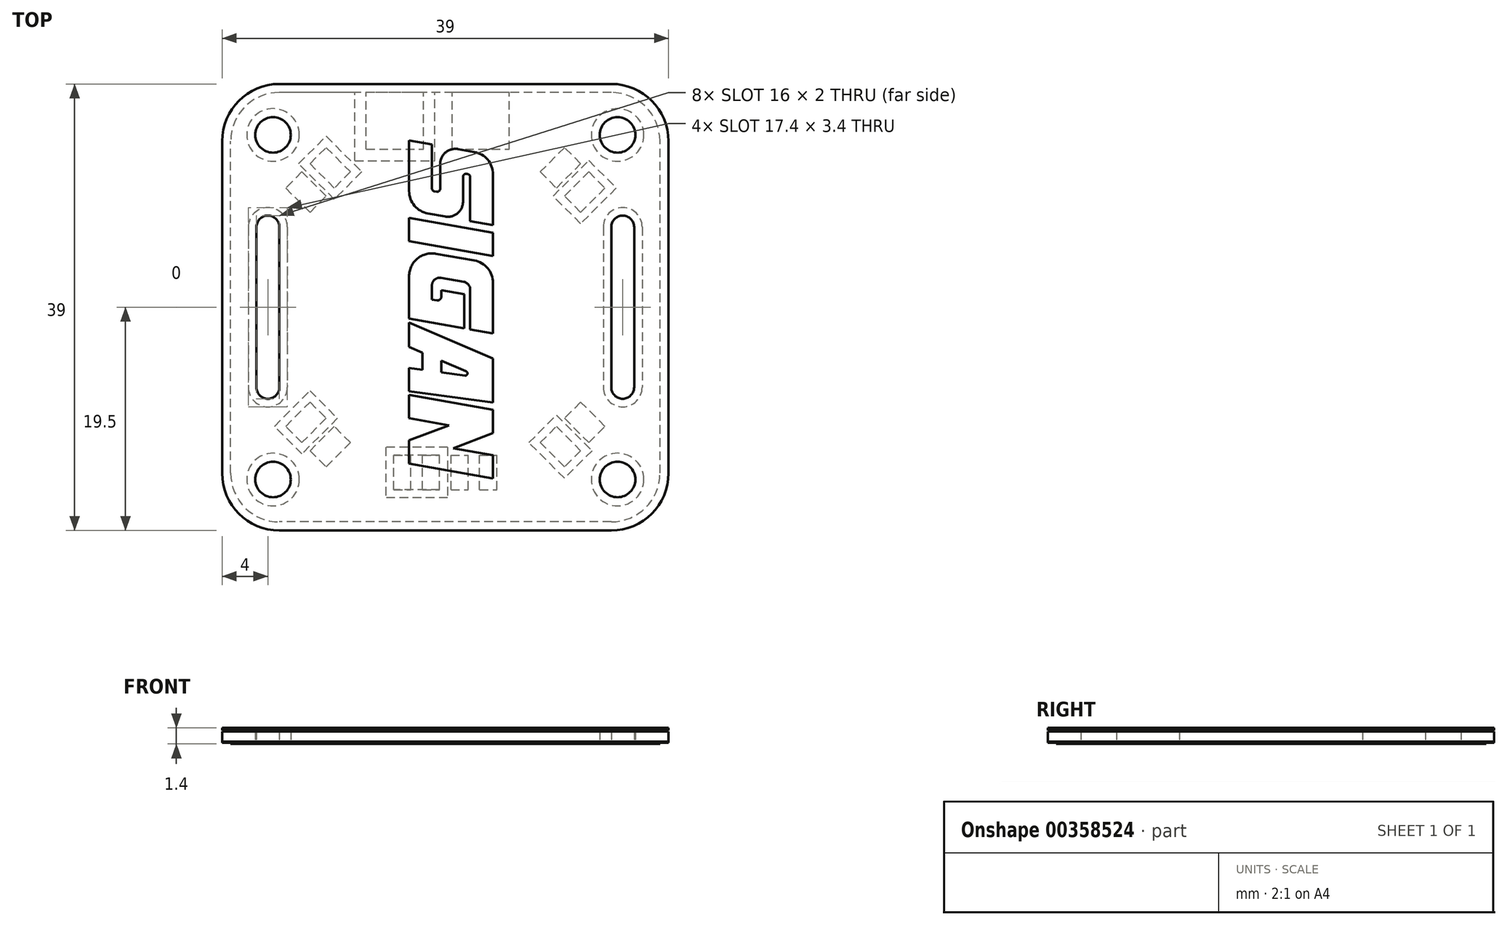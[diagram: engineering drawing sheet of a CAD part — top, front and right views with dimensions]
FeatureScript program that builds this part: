
annotation { "Feature Type Name" : "Feature", "Feature Type Description" : "" }
export const myFeature = defineFeature(function(context is Context, id is Id, definition is map)
    precondition{}
    {
        {
            var Q0;
            Q0=qCreatedBy(makeId("Top.planeOp"),FACE);
            var sketch = newSketch(context, id + "F0", { "sketchPlane" : qUnion([Q0])});
            skLineSegment(sketch, "E0.bottom", {"start": v(14.5, -19.5) * mm, "end": v(-14.5, -19.5) * mm});
            skLineSegment(sketch, "E0.top", {"start": v(14.5, 19.5) * mm, "end": v(7.5, 19.5) * mm});
            skLineSegment(sketch, "E0.left", {"start": v(19.5, -14.5) * mm, "end": v(19.5, 14.5) * mm});
            skLineSegment(sketch, "E0.right", {"start": v(-19.5, -14.5) * mm, "end": v(-19.5, 14.5) * mm});
            skPoint(sketch, "E0.middle", {"position": v(0, 0) * mm});
            skPoint(sketch, "E1.visualSharp", {"position": v(19.5, -19.5) * mm});
            skArc(sketch, "E1.filletArc", {"start": v(14.5, -19.5) * mm, "mid": v(18.04, -18.04) * mm, "end": v(19.5, -14.5) * mm});
            skPoint(sketch, "E2.visualSharp", {"position": v(-19.5, -19.5) * mm});
            skArc(sketch, "E2.filletArc", {"start": v(-19.5, -14.5) * mm, "mid": v(-18.04, -18.04) * mm, "end": v(-14.5, -19.5) * mm});
            skPoint(sketch, "E3.visualSharp", {"position": v(-19.5, 19.5) * mm});
            skArc(sketch, "E3.filletArc", {"start": v(-14.5, 19.5) * mm, "mid": v(-18.04, 18.04) * mm, "end": v(-19.5, 14.5) * mm});
            skPoint(sketch, "E4.visualSharp", {"position": v(19.5, 19.5) * mm});
            skArc(sketch, "E4.filletArc", {"start": v(19.5, 14.5) * mm, "mid": v(18.04, 18.04) * mm, "end": v(14.5, 19.5) * mm});
            skLineSegment(sketch, "E5", {"start": v(-7.5, 19.5) * mm, "end": v(-7.5, 19.5) * mm});
            skLineSegment(sketch, "E6", {"start": v(-7.5, 19.5) * mm, "end": v(7.5, 19.5) * mm});
            skLineSegment(sketch, "E7", {"start": v(7.5, 19.5) * mm, "end": v(7.5, 19.5) * mm});
            skLineSegment(sketch, "E8.trimOffspring", {"start": v(-7.5, 19.5) * mm, "end": v(-14.5, 19.5) * mm});
            skLineSegment(sketch, "E9", {"start": v(0, 19.5) * mm, "end": v(0, 0) * mm, "construction": true});
            skLineSegment(sketch, "E10.left", {"start": v(-16.5, 7) * mm, "end": v(-16.5, -7) * mm});
            skLineSegment(sketch, "E10.right", {"start": v(-14.5, 7) * mm, "end": v(-14.5, -7) * mm});
            skPoint(sketch, "E10.middle", {"position": v(-15.5, 0) * mm});
            skArc(sketch, "E11", {"start": v(-14.5, 7) * mm, "mid": v(-15.5, 8) * mm, "end": v(-16.5, 7) * mm});
            skArc(sketch, "E12", {"start": v(-16.5, -7) * mm, "mid": v(-15.5, -8) * mm, "end": v(-14.5, -7) * mm});
            skArc(sketch, "E13.MirrorCS", {"start": v(16.5, -7) * mm, "mid": v(15.5, -8) * mm, "end": v(14.5, -7) * mm});
            skArc(sketch, "E14.MirrorCS", {"start": v(14.5, 7) * mm, "mid": v(15.5, 8) * mm, "end": v(16.5, 7) * mm});
            skPoint(sketch, "E15.MirrorP", {"position": v(15.5, 0) * mm});
            skLineSegment(sketch, "E16.MirrorCS", {"start": v(16.5, 7) * mm, "end": v(16.5, -7) * mm});
            skLineSegment(sketch, "E17.MirrorCS", {"start": v(14.5, 7) * mm, "end": v(14.5, -7) * mm});
            skCircle(sketch, "E18.0", {"center": v(-15.05, 15.05) * mm, "radius": 1.55 * mm});
            skCircle(sketch, "E18.1", {"center": v(15.05, 15.05) * mm, "radius": 1.55 * mm});
            skCircle(sketch, "E18.2", {"center": v(15.05, -15.05) * mm, "radius": 1.55 * mm});
            skCircle(sketch, "E18.3", {"center": v(-15.05, -15.05) * mm, "radius": 1.55 * mm});
            skSolve(sketch);
        }
        {
            var Q0;
            {var subQ0=makeQuery(id+"FaKBFoj8S7sMaQz_0.opExtrude","CAP_EDGE",EDGE,{"disambiguationData":[OSD([sQuery(id+"FUyg42RqR56omhc_0.wireOp",EDGE,"1f71cb04-1cd7-49c8-8af8-68a2ebdd6a70.filletArc")])],"isStart":true});Q0=makeQuery(id+"F0.imprint","IMPRINT",FACE,{"disambiguationData":[TD([[makeQuery(id+"F0.imprint","IMPRINT",EDGE,{"derivedFrom":subQ0}),-1.0]])]});}
            var Q1;
            Q1=makeQuery(id+"F0.imprint","IMPRINT",FACE,{"disambiguationData":[TD([[makeQuery(id+"F0.imprint","IMPRINT",EDGE,{"derivedFrom":sQuery(id+"F0.wireOp",EDGE,"E0.bottom")}),-1.0]])]});
            var Q2;
            {var subQ0=makeQuery(id+"FaKBFoj8S7sMaQz_0.opExtrude","CAP_EDGE",EDGE,{"disambiguationData":[OSD([sQuery(id+"FUyg42RqR56omhc_0.wireOp",EDGE,"45a09e78-3408-4181-94d1-7675ea45a7b5.0")])],"isStart":true});Q2=makeQuery(id+"F0.imprint","IMPRINT",FACE,{"disambiguationData":[TD([[makeQuery(id+"F0.imprint","IMPRINT",EDGE,{"derivedFrom":subQ0}),1.0]])]});}
            extrude(context, id + "F1", {"entities" : qUnion([Q0, Q1, Q2]), "depth" : 1 * mm});
        }
        {
            var Q0;
            Q0=makeQuery(id+"F1.opExtrude","SWEPT_BODY",BODY,{"disambiguationData":[OSD([sQuery(id+"FUyg42RqR56omhc_0.wireOp",EDGE,"apNCEg5n-BcgS-b9KA-570i-48yKU28l5lF8"),sQuery(id+"F0.wireOp",EDGE,"E0.bottom"),sQuery(id+"F0.wireOp",EDGE,"E0.top"),sQuery(id+"F0.wireOp",EDGE,"E0.left"),sQuery(id+"F0.wireOp",EDGE,"E0.right"),sQuery(id+"F0.wireOp",EDGE,"E1.filletArc"),sQuery(id+"F0.wireOp",EDGE,"E2.filletArc"),sQuery(id+"F0.wireOp",EDGE,"E3.filletArc"),sQuery(id+"F0.wireOp",EDGE,"E4.filletArc")])]});
            var Q1;
            Q1=qCreatedBy(makeId("Top.planeOp"),FACE);
            transform(context, id + "F2", {"entities" : qUnion([Q0]), "transformType" : TransformType.TRANSLATION_DISTANCE, "transformDirection" : qUnion([Q1]), "distance" : 6 * mm, "oppositeDirection" : true, "makeCopy" : false});
        }
        {
            var Q0;
            Q0=makeQuery(id+"F1.opExtrude","CAP_FACE",FACE,{"disambiguationData":[OSD([sQuery(id+"FUyg42RqR56omhc_0.wireOp",EDGE,"apNCEg5n-BcgS-b9KA-570i-48yKU28l5lF8"),sQuery(id+"F0.wireOp",EDGE,"E0.bottom"),sQuery(id+"F0.wireOp",EDGE,"E0.top"),sQuery(id+"F0.wireOp",EDGE,"E0.left"),sQuery(id+"F0.wireOp",EDGE,"E0.right"),sQuery(id+"F0.wireOp",EDGE,"E1.filletArc"),sQuery(id+"F0.wireOp",EDGE,"E2.filletArc"),sQuery(id+"F0.wireOp",EDGE,"E3.filletArc"),sQuery(id+"F0.wireOp",EDGE,"E4.filletArc"),sQuery(id+"F0.wireOp",EDGE,"E5"),sQuery(id+"F0.wireOp",EDGE,"E6"),sQuery(id+"F0.wireOp",EDGE,"E7"),sQuery(id+"F0.wireOp",EDGE,"E8.trimOffspring"),sQuery(id+"F0.wireOp",EDGE,"E10.left"),sQuery(id+"F0.wireOp",EDGE,"E10.right"),sQuery(id+"F0.wireOp",EDGE,"E11"),sQuery(id+"F0.wireOp",EDGE,"E12"),sQuery(id+"F0.wireOp",EDGE,"E13.MirrorCS"),sQuery(id+"F0.wireOp",EDGE,"E14.MirrorCS"),sQuery(id+"F0.wireOp",EDGE,"E16.MirrorCS"),sQuery(id+"F0.wireOp",EDGE,"E17.MirrorCS")])],"isStart":true});
            var sketch = newSketch(context, id + "F3", { "sketchPlane" : qUnion([Q0])});
            skLineSegment(sketch, "E19.bottom", {"start": v(0.6, -13.8) * mm, "end": v(5.6, -13.8) * mm});
            skLineSegment(sketch, "E19.top", {"start": v(0.6, -18.8) * mm, "end": v(5.6, -18.8) * mm});
            skLineSegment(sketch, "E19.left", {"start": v(0.6, -13.8) * mm, "end": v(0.6, -18.8) * mm});
            skLineSegment(sketch, "E19.right", {"start": v(5.6, -13.8) * mm, "end": v(5.6, -18.8) * mm});
            skPoint(sketch, "E19.middle", {"position": v(3.1, -16.3) * mm});
            skLineSegment(sketch, "E20.1.0.0", {"start": v(-1.9, -13.8) * mm, "end": v(-1.9, -18.8) * mm});
            skLineSegment(sketch, "E20.1.0.1", {"start": v(-6.9, -13.8) * mm, "end": v(-1.9, -13.8) * mm});
            skLineSegment(sketch, "E20.1.0.2", {"start": v(-6.9, -18.8) * mm, "end": v(-1.9, -18.8) * mm});
            skLineSegment(sketch, "E20.1.0.3", {"start": v(-6.9, -13.8) * mm, "end": v(-6.9, -18.8) * mm});
            skPoint(sketch, "E20.1.0.4", {"position": v(-4.4, -16.3) * mm});
            skLineSegment(sketch, "E20.direction1", {"start": v(0.6, -18.8) * mm, "end": v(-6.9, -18.8) * mm, "construction": true});
            skLineSegment(sketch, "E21", {"start": v(13.95, -10.41) * mm, "end": v(11.83, -8.29) * mm});
            skLineSegment(sketch, "E22", {"start": v(11.83, -8.29) * mm, "end": v(10.41, -9.7) * mm});
            skLineSegment(sketch, "E23", {"start": v(10.41, -9.7) * mm, "end": v(12.53, -11.83) * mm});
            skLineSegment(sketch, "E24", {"start": v(12.53, -11.83) * mm, "end": v(13.95, -10.41) * mm});
            skPoint(sketch, "E25.center", {"position": v(0, 0) * mm});
            skLineSegment(sketch, "E26", {"start": v(0, 0) * mm, "end": v(0, -24.64) * mm, "construction": true});
            skLineSegment(sketch, "E27", {"start": v(0, 0) * mm, "end": v(21.38, -21.38) * mm, "construction": true});
            skLineSegment(sketch, "E28.MirrorCS", {"start": v(8.29, -11.83) * mm, "end": v(9.7, -10.41) * mm});
            skLineSegment(sketch, "E29.MirrorCS", {"start": v(9.7, -10.41) * mm, "end": v(11.83, -12.53) * mm});
            skLineSegment(sketch, "E30.MirrorCS", {"start": v(10.41, -13.95) * mm, "end": v(8.29, -11.83) * mm});
            skLineSegment(sketch, "E31.MirrorCS", {"start": v(11.83, -12.53) * mm, "end": v(10.41, -13.95) * mm});
            skLineSegment(sketch, "E32.1.0", {"start": v(-8.29, -11.83) * mm, "end": v(-9.7, -10.41) * mm});
            skLineSegment(sketch, "E32.1.1", {"start": v(-11.83, -8.29) * mm, "end": v(-10.41, -9.7) * mm});
            skLineSegment(sketch, "E32.1.2", {"start": v(-10.41, -9.7) * mm, "end": v(-12.53, -11.83) * mm});
            skLineSegment(sketch, "E32.1.3", {"start": v(-9.7, -10.41) * mm, "end": v(-11.83, -12.53) * mm});
            skLineSegment(sketch, "E32.1.4", {"start": v(-11.83, -12.53) * mm, "end": v(-10.41, -13.95) * mm});
            skLineSegment(sketch, "E32.1.5", {"start": v(-12.53, -11.83) * mm, "end": v(-13.95, -10.41) * mm});
            skLineSegment(sketch, "E32.1.6", {"start": v(-10.41, -13.95) * mm, "end": v(-8.29, -11.83) * mm});
            skLineSegment(sketch, "E32.1.7", {"start": v(-13.95, -10.41) * mm, "end": v(-11.83, -8.29) * mm});
            skLineSegment(sketch, "E32.2.0", {"start": v(-11.83, 8.29) * mm, "end": v(-10.41, 9.7) * mm});
            skLineSegment(sketch, "E32.2.1", {"start": v(-8.29, 11.83) * mm, "end": v(-9.7, 10.41) * mm});
            skLineSegment(sketch, "E32.2.2", {"start": v(-9.7, 10.41) * mm, "end": v(-11.83, 12.53) * mm});
            skLineSegment(sketch, "E32.2.3", {"start": v(-10.41, 9.7) * mm, "end": v(-12.53, 11.83) * mm});
            skLineSegment(sketch, "E32.2.4", {"start": v(-12.53, 11.83) * mm, "end": v(-13.95, 10.41) * mm});
            skLineSegment(sketch, "E32.2.5", {"start": v(-11.83, 12.53) * mm, "end": v(-10.41, 13.95) * mm});
            skLineSegment(sketch, "E32.2.6", {"start": v(-13.95, 10.41) * mm, "end": v(-11.83, 8.29) * mm});
            skLineSegment(sketch, "E32.2.7", {"start": v(-10.41, 13.95) * mm, "end": v(-8.29, 11.83) * mm});
            skLineSegment(sketch, "E32.3.0", {"start": v(8.29, 11.83) * mm, "end": v(9.7, 10.41) * mm});
            skLineSegment(sketch, "E32.3.1", {"start": v(11.83, 8.29) * mm, "end": v(10.41, 9.7) * mm});
            skLineSegment(sketch, "E32.3.2", {"start": v(10.41, 9.7) * mm, "end": v(12.53, 11.83) * mm});
            skLineSegment(sketch, "E32.3.3", {"start": v(9.7, 10.41) * mm, "end": v(11.83, 12.53) * mm});
            skLineSegment(sketch, "E32.3.4", {"start": v(11.83, 12.53) * mm, "end": v(10.41, 13.95) * mm});
            skLineSegment(sketch, "E32.3.5", {"start": v(12.53, 11.83) * mm, "end": v(13.95, 10.41) * mm});
            skLineSegment(sketch, "E32.3.6", {"start": v(10.41, 13.95) * mm, "end": v(8.29, 11.83) * mm});
            skLineSegment(sketch, "E32.3.7", {"start": v(13.95, 10.41) * mm, "end": v(11.83, 8.29) * mm});
            skLineSegment(sketch, "E32.anchor1", {"start": v(0, 0) * mm, "end": v(10.41, -13.95) * mm, "construction": true});
            skLineSegment(sketch, "E32.anchor2", {"start": v(0, 0) * mm, "end": v(13.95, 10.41) * mm, "construction": true});
            skLineSegment(sketch, "E33.bottom", {"start": v(3, 15.94) * mm, "end": v(4.5, 15.94) * mm});
            skLineSegment(sketch, "E33.top", {"start": v(3, 12.94) * mm, "end": v(4.5, 12.94) * mm});
            skLineSegment(sketch, "E33.left", {"start": v(3, 15.94) * mm, "end": v(3, 12.94) * mm});
            skLineSegment(sketch, "E33.right", {"start": v(4.5, 15.94) * mm, "end": v(4.5, 12.94) * mm});
            skPoint(sketch, "E33.middle", {"position": v(3.75, 14.44) * mm});
            skPoint(sketch, "E34.1.0.0", {"position": v(1.25, 14.44) * mm});
            skLineSegment(sketch, "E34.1.0.1", {"start": v(0.5, 12.94) * mm, "end": v(2, 12.94) * mm});
            skLineSegment(sketch, "E34.1.0.2", {"start": v(2, 15.94) * mm, "end": v(2, 12.94) * mm});
            skLineSegment(sketch, "E34.1.0.3", {"start": v(0.5, 15.94) * mm, "end": v(0.5, 12.94) * mm});
            skLineSegment(sketch, "E34.1.0.4", {"start": v(0.5, 15.94) * mm, "end": v(2, 15.94) * mm});
            skPoint(sketch, "E34.2.0.0", {"position": v(-1.25, 14.44) * mm});
            skLineSegment(sketch, "E34.2.0.1", {"start": v(-2, 12.94) * mm, "end": v(-0.5, 12.94) * mm});
            skLineSegment(sketch, "E34.2.0.2", {"start": v(-0.5, 15.94) * mm, "end": v(-0.5, 12.94) * mm});
            skLineSegment(sketch, "E34.2.0.3", {"start": v(-2, 15.94) * mm, "end": v(-2, 12.94) * mm});
            skLineSegment(sketch, "E34.2.0.4", {"start": v(-2, 15.94) * mm, "end": v(-0.5, 15.94) * mm});
            skPoint(sketch, "E34.3.0.0", {"position": v(-3.75, 14.44) * mm});
            skLineSegment(sketch, "E34.3.0.1", {"start": v(-4.5, 12.94) * mm, "end": v(-3, 12.94) * mm});
            skLineSegment(sketch, "E34.3.0.2", {"start": v(-3, 15.94) * mm, "end": v(-3, 12.94) * mm});
            skLineSegment(sketch, "E34.3.0.3", {"start": v(-4.5, 15.94) * mm, "end": v(-4.5, 12.94) * mm});
            skLineSegment(sketch, "E34.3.0.4", {"start": v(-4.5, 15.94) * mm, "end": v(-3, 15.94) * mm});
            skLineSegment(sketch, "E34.direction1", {"start": v(3, 12.94) * mm, "end": v(0.5, 12.94) * mm, "construction": true});
            skSolve(sketch);
        }
        {
            var Q0;
            Q0=makeQuery(id+"F3.imprint","IMPRINT",FACE,{"disambiguationData":[TD([[makeQuery(id+"F3.imprint","IMPRINT",EDGE,{"derivedFrom":sQuery(id+"F3.wireOp",EDGE,"E19.bottom")}),1.0]])]});
            extrude(context, id + "F4", {"entities" : qUnion([Q0]), "depth" : .1 * mm});
        }
        {
            var Q0;
            Q0=makeQuery(id+"F1.opExtrude","CAP_FACE",FACE,{"disambiguationData":[OSD([sQuery(id+"FUyg42RqR56omhc_0.wireOp",EDGE,"apNCEg5n-BcgS-b9KA-570i-48yKU28l5lF8"),sQuery(id+"F0.wireOp",EDGE,"E0.bottom"),sQuery(id+"F0.wireOp",EDGE,"E0.top"),sQuery(id+"F0.wireOp",EDGE,"E0.left"),sQuery(id+"F0.wireOp",EDGE,"E0.right"),sQuery(id+"F0.wireOp",EDGE,"E1.filletArc"),sQuery(id+"F0.wireOp",EDGE,"E2.filletArc"),sQuery(id+"F0.wireOp",EDGE,"E3.filletArc"),sQuery(id+"F0.wireOp",EDGE,"E4.filletArc"),sQuery(id+"F0.wireOp",EDGE,"E5"),sQuery(id+"F0.wireOp",EDGE,"E6"),sQuery(id+"F0.wireOp",EDGE,"E7"),sQuery(id+"F0.wireOp",EDGE,"E8.trimOffspring"),sQuery(id+"F0.wireOp",EDGE,"E10.left"),sQuery(id+"F0.wireOp",EDGE,"E10.right"),sQuery(id+"F0.wireOp",EDGE,"E11"),sQuery(id+"F0.wireOp",EDGE,"E12"),sQuery(id+"F0.wireOp",EDGE,"E13.MirrorCS"),sQuery(id+"F0.wireOp",EDGE,"E14.MirrorCS"),sQuery(id+"F0.wireOp",EDGE,"E16.MirrorCS"),sQuery(id+"F0.wireOp",EDGE,"E17.MirrorCS")])],"isStart":true});
            var sketch = newSketch(context, id + "F5", { "sketchPlane" : qUnion([Q0])});
            skLineSegment(sketch, "E35.0", {"start": v(9.42, -9.7) * mm, "end": v(12.53, -12.82) * mm});
            skLineSegment(sketch, "E35.1", {"start": v(11.83, -7.3) * mm, "end": v(9.42, -9.7) * mm});
            skLineSegment(sketch, "E35.2", {"start": v(14.94, -10.41) * mm, "end": v(11.83, -7.3) * mm});
            skLineSegment(sketch, "E35.3", {"start": v(12.53, -12.82) * mm, "end": v(14.94, -10.41) * mm});
            skLineSegment(sketch, "E36.1.0", {"start": v(7.3, 11.83) * mm, "end": v(9.7, 9.42) * mm});
            skLineSegment(sketch, "E36.1.1", {"start": v(9.7, 9.42) * mm, "end": v(12.82, 12.53) * mm});
            skLineSegment(sketch, "E36.1.2", {"start": v(10.41, 14.94) * mm, "end": v(7.3, 11.83) * mm});
            skLineSegment(sketch, "E36.1.3", {"start": v(12.82, 12.53) * mm, "end": v(10.41, 14.94) * mm});
            skLineSegment(sketch, "E36.2.0", {"start": v(-11.83, 7.3) * mm, "end": v(-9.42, 9.7) * mm});
            skLineSegment(sketch, "E36.2.1", {"start": v(-9.42, 9.7) * mm, "end": v(-12.53, 12.82) * mm});
            skLineSegment(sketch, "E36.2.2", {"start": v(-14.94, 10.41) * mm, "end": v(-11.83, 7.3) * mm});
            skLineSegment(sketch, "E36.2.3", {"start": v(-12.53, 12.82) * mm, "end": v(-14.94, 10.41) * mm});
            skLineSegment(sketch, "E36.3.0", {"start": v(-7.3, -11.83) * mm, "end": v(-9.7, -9.42) * mm});
            skLineSegment(sketch, "E36.3.1", {"start": v(-9.7, -9.42) * mm, "end": v(-12.82, -12.53) * mm});
            skLineSegment(sketch, "E36.3.2", {"start": v(-10.41, -14.94) * mm, "end": v(-7.9, -12.43) * mm});
            skLineSegment(sketch, "E36.3.3", {"start": v(-12.82, -12.53) * mm, "end": v(-10.41, -14.94) * mm});
            skPoint(sketch, "E36.center", {"position": v(0, 0) * mm});
            skLineSegment(sketch, "E37.0", {"start": v(-0.9, -12.8) * mm, "end": v(-0.9, -19.5) * mm});
            skLineSegment(sketch, "E37.1", {"start": v(-7.9, -12.8) * mm, "end": v(-0.9, -12.8) * mm});
            skLineSegment(sketch, "E37.2", {"start": v(-7.9, -12.8) * mm, "end": v(-7.9, -19.5) * mm});
            skLineSegment(sketch, "E38.0", {"start": v(14.5, -19.5) * mm, "end": v(-14.5, -19.5) * mm});
            skLineSegment(sketch, "E39.trimOffspring", {"start": v(-7.9, -12.43) * mm, "end": v(-7.3, -11.83) * mm});
            skArc(sketch, "E40.0", {"start": v(18.75, -14.5) * mm, "mid": v(17.5, -17.5) * mm, "end": v(14.5, -18.75) * mm});
            skLineSegment(sketch, "E40.1", {"start": v(18.75, 14.5) * mm, "end": v(18.75, -14.5) * mm});
            skLineSegment(sketch, "E40.2", {"start": v(14.5, -18.75) * mm, "end": v(-14.5, -18.75) * mm});
            skArc(sketch, "E40.3", {"start": v(14.5, 18.75) * mm, "mid": v(17.5, 17.5) * mm, "end": v(18.75, 14.5) * mm});
            skArc(sketch, "E40.4", {"start": v(-14.5, -18.75) * mm, "mid": v(-17.5, -17.5) * mm, "end": v(-18.75, -14.5) * mm});
            skLineSegment(sketch, "E40.5", {"start": v(-18.75, 14.5) * mm, "end": v(-18.75, -14.5) * mm});
            skArc(sketch, "E40.6", {"start": v(-18.75, 14.5) * mm, "mid": v(-17.5, 17.5) * mm, "end": v(-14.5, 18.75) * mm});
            skLineSegment(sketch, "E40.7", {"start": v(14.5, 18.75) * mm, "end": v(-14.5, 18.75) * mm});
            skCircle(sketch, "E41.0", {"center": v(15.05, -15.05) * mm, "radius": 2.3 * mm});
            skCircle(sketch, "E42.0", {"center": v(-15.05, -15.05) * mm, "radius": 2.3 * mm});
            skCircle(sketch, "E43.0", {"center": v(-15.05, 15.05) * mm, "radius": 2.3 * mm});
            skCircle(sketch, "E44.0", {"center": v(15.05, 15.05) * mm, "radius": 2.3 * mm});
            skArc(sketch, "E45.0", {"start": v(13.8, -7) * mm, "mid": v(15.5, -8.7) * mm, "end": v(17.2, -7) * mm});
            skLineSegment(sketch, "E45.1", {"start": v(13.8, -7) * mm, "end": v(13.8, 7) * mm});
            skArc(sketch, "E45.2", {"start": v(17.2, 7) * mm, "mid": v(15.5, 8.7) * mm, "end": v(13.8, 7) * mm});
            skLineSegment(sketch, "E45.3", {"start": v(17.2, -7) * mm, "end": v(17.2, 7) * mm});
            skLineSegment(sketch, "E46.0", {"start": v(-13.8, -7) * mm, "end": v(-13.8, 7) * mm});
            skArc(sketch, "E46.1", {"start": v(-13.8, -7) * mm, "mid": v(-15.5, -8.7) * mm, "end": v(-17.2, -7) * mm});
            skLineSegment(sketch, "E46.2", {"start": v(-17.2, -7) * mm, "end": v(-17.2, 7) * mm});
            skArc(sketch, "E46.3", {"start": v(-17.2, 7) * mm, "mid": v(-15.5, 8.7) * mm, "end": v(-13.8, 7) * mm});
            skLineSegment(sketch, "E47.0", {"start": v(10.41, -9.7) * mm, "end": v(12.53, -11.83) * mm});
            skLineSegment(sketch, "E47.1", {"start": v(12.53, -11.83) * mm, "end": v(13.95, -10.41) * mm});
            skLineSegment(sketch, "E47.2", {"start": v(13.95, -10.41) * mm, "end": v(11.83, -8.29) * mm});
            skLineSegment(sketch, "E47.3", {"start": v(11.83, -8.29) * mm, "end": v(10.41, -9.7) * mm});
            skLineSegment(sketch, "E47.4", {"start": v(-10.41, -13.95) * mm, "end": v(-8.29, -11.83) * mm});
            skLineSegment(sketch, "E47.5", {"start": v(-11.83, -12.53) * mm, "end": v(-10.41, -13.95) * mm});
            skLineSegment(sketch, "E47.6", {"start": v(-9.7, -10.41) * mm, "end": v(-11.83, -12.53) * mm});
            skLineSegment(sketch, "E47.7", {"start": v(-8.29, -11.83) * mm, "end": v(-9.7, -10.41) * mm});
            skLineSegment(sketch, "E47.8", {"start": v(-13.95, 10.41) * mm, "end": v(-11.83, 8.29) * mm});
            skLineSegment(sketch, "E47.9", {"start": v(-11.83, 8.29) * mm, "end": v(-10.41, 9.7) * mm});
            skLineSegment(sketch, "E47.10", {"start": v(-12.53, 11.83) * mm, "end": v(-13.95, 10.41) * mm});
            skLineSegment(sketch, "E47.11", {"start": v(-10.41, 9.7) * mm, "end": v(-12.53, 11.83) * mm});
            skLineSegment(sketch, "E47.12", {"start": v(9.7, 10.41) * mm, "end": v(11.83, 12.53) * mm});
            skLineSegment(sketch, "E47.13", {"start": v(8.29, 11.83) * mm, "end": v(9.7, 10.41) * mm});
            skLineSegment(sketch, "E47.14", {"start": v(10.41, 13.95) * mm, "end": v(8.29, 11.83) * mm});
            skLineSegment(sketch, "E47.15", {"start": v(11.83, 12.53) * mm, "end": v(10.41, 13.95) * mm});
            skLineSegment(sketch, "E48.0", {"start": v(-1.9, -13.8) * mm, "end": v(-1.9, -18.8) * mm});
            skLineSegment(sketch, "E48.1", {"start": v(-6.9, -13.8) * mm, "end": v(-1.9, -13.8) * mm});
            skLineSegment(sketch, "E48.2", {"start": v(-6.9, -13.8) * mm, "end": v(-6.9, -18.8) * mm});
            skLineSegment(sketch, "E48.3", {"start": v(-6.9, -18.8) * mm, "end": v(-1.9, -18.8) * mm});
            skLineSegment(sketch, "E49.bottom", {"start": v(0.2, 12.24) * mm, "end": v(-5.2, 12.24) * mm});
            skLineSegment(sketch, "E49.top", {"start": v(0.2, 16.64) * mm, "end": v(-5.2, 16.64) * mm});
            skLineSegment(sketch, "E49.left", {"start": v(0.2, 12.24) * mm, "end": v(0.2, 16.64) * mm});
            skLineSegment(sketch, "E49.right", {"start": v(-5.2, 12.24) * mm, "end": v(-5.2, 16.64) * mm});
            skLineSegment(sketch, "E50.bottom", {"start": v(-0.5, 12.94) * mm, "end": v(-4.5, 12.94) * mm});
            skLineSegment(sketch, "E50.top", {"start": v(-0.5, 15.94) * mm, "end": v(-4.5, 15.94) * mm});
            skLineSegment(sketch, "E50.left", {"start": v(-0.5, 12.94) * mm, "end": v(-0.5, 15.94) * mm});
            skLineSegment(sketch, "E50.right", {"start": v(-4.5, 12.94) * mm, "end": v(-4.5, 15.94) * mm});
            skSolve(sketch);
        }
        {
            var Q0;
            Q0=makeQuery(id+"F5.imprint","IMPRINT",FACE,{"disambiguationData":[TD([[makeQuery(id+"F5.imprint","IMPRINT",EDGE,{"derivedFrom":sQuery(id+"F5.wireOp",EDGE,"E35.0")}),-1.0]])]});
            var Q1;
            Q1=makeQuery(id+"F5.imprint","IMPRINT",FACE,{"disambiguationData":[TD([[makeQuery(id+"F5.imprint","IMPRINT",EDGE,{"derivedFrom":sQuery(id+"F5.wireOp",EDGE,"E47.0")}),1.0]])]});
            var Q2;
            Q2=makeQuery(id+"F5.imprint","IMPRINT",FACE,{"disambiguationData":[TD([[makeQuery(id+"F5.imprint","IMPRINT",EDGE,{"derivedFrom":sQuery(id+"F5.wireOp",EDGE,"E47.4")}),1.0]])]});
            var Q3;
            Q3=makeQuery(id+"F5.imprint","IMPRINT",FACE,{"disambiguationData":[TD([[makeQuery(id+"F5.imprint","IMPRINT",EDGE,{"derivedFrom":sQuery(id+"F5.wireOp",EDGE,"E47.8")}),1.0]])]});
            var Q4;
            Q4=makeQuery(id+"F5.imprint","IMPRINT",FACE,{"disambiguationData":[TD([[makeQuery(id+"F5.imprint","IMPRINT",EDGE,{"derivedFrom":sQuery(id+"F5.wireOp",EDGE,"E47.12")}),1.0]])]});
            var Q5;
            {var subQ5=sQuery(id+"F5.wireOp",EDGE,"E48.1");Q5=makeQuery(id+"F5.imprint","IMPRINT",FACE,{"disambiguationData":[TD([[makeQuery(id+"F5.imprint","IMPRINT",EDGE,{"derivedFrom":subQ5}),-1.0]])]});}
            var Q6;
            Q6=makeQuery(id+"F5.imprint","IMPRINT",FACE,{"disambiguationData":[TD([[makeQuery(id+"F5.imprint","IMPRINT",EDGE,{"derivedFrom":sQuery(id+"F5.wireOp",EDGE,"E50.bottom")}),-1.0]])]});
            extrude(context, id + "F6", {"entities" : qUnion([Q0, Q1, Q2, Q3, Q4, Q5, Q6]), "depth" : .1 * mm});
        }
        {
            var Q0;
            Q0=makeQuery(id+"F4.opExtrude","SWEPT_BODY",BODY,{"disambiguationData":[OSD([sQuery(id+"FUyg42RqR56omhc_0.wireOp",EDGE,"apNCEg5n-BcgS-b9KA-570i-48yKU28l5lF8"),sQuery(id+"F0.wireOp",EDGE,"E0.bottom"),sQuery(id+"F0.wireOp",EDGE,"E0.top"),sQuery(id+"F0.wireOp",EDGE,"E0.left"),sQuery(id+"F0.wireOp",EDGE,"E0.right"),sQuery(id+"F0.wireOp",EDGE,"E1.filletArc"),sQuery(id+"F0.wireOp",EDGE,"E2.filletArc"),sQuery(id+"F0.wireOp",EDGE,"E3.filletArc"),sQuery(id+"F0.wireOp",EDGE,"E4.filletArc"),sQuery(id+"F0.wireOp",EDGE,"E5"),sQuery(id+"F0.wireOp",EDGE,"E6"),sQuery(id+"F0.wireOp",EDGE,"E7"),sQuery(id+"F0.wireOp",EDGE,"E8.trimOffspring"),sQuery(id+"F0.wireOp",EDGE,"E10.left"),sQuery(id+"F0.wireOp",EDGE,"E10.right"),sQuery(id+"F0.wireOp",EDGE,"E11"),sQuery(id+"F0.wireOp",EDGE,"E12"),sQuery(id+"F0.wireOp",EDGE,"E13.MirrorCS"),sQuery(id+"F0.wireOp",EDGE,"E14.MirrorCS"),sQuery(id+"F0.wireOp",EDGE,"E16.MirrorCS"),sQuery(id+"F0.wireOp",EDGE,"E17.MirrorCS"),sQuery(id+"F3.wireOp",EDGE,"E19.bottom"),sQuery(id+"F3.wireOp",EDGE,"E19.top"),sQuery(id+"F3.wireOp",EDGE,"E19.left"),sQuery(id+"F3.wireOp",EDGE,"E19.right"),sQuery(id+"F3.wireOp",EDGE,"E20.1.0.0"),sQuery(id+"F3.wireOp",EDGE,"E20.1.0.1"),sQuery(id+"F3.wireOp",EDGE,"E20.1.0.2"),sQuery(id+"F3.wireOp",EDGE,"E20.1.0.3"),sQuery(id+"F3.wireOp",EDGE,"E21"),sQuery(id+"F3.wireOp",EDGE,"E22"),sQuery(id+"F3.wireOp",EDGE,"E23"),sQuery(id+"F3.wireOp",EDGE,"E24"),sQuery(id+"F3.wireOp",EDGE,"E28.MirrorCS"),sQuery(id+"F3.wireOp",EDGE,"E29.MirrorCS"),sQuery(id+"F3.wireOp",EDGE,"E30.MirrorCS"),sQuery(id+"F3.wireOp",EDGE,"E31.MirrorCS"),sQuery(id+"F3.wireOp",EDGE,"E32.1.0"),sQuery(id+"F3.wireOp",EDGE,"E32.1.1"),sQuery(id+"F3.wireOp",EDGE,"E32.1.2"),sQuery(id+"F3.wireOp",EDGE,"E32.1.3"),sQuery(id+"F3.wireOp",EDGE,"E32.1.4"),sQuery(id+"F3.wireOp",EDGE,"E32.1.5"),sQuery(id+"F3.wireOp",EDGE,"E32.1.6"),sQuery(id+"F3.wireOp",EDGE,"E32.1.7"),sQuery(id+"F3.wireOp",EDGE,"E32.2.0"),sQuery(id+"F3.wireOp",EDGE,"E32.2.1"),sQuery(id+"F3.wireOp",EDGE,"E32.2.2"),sQuery(id+"F3.wireOp",EDGE,"E32.2.3"),sQuery(id+"F3.wireOp",EDGE,"E32.2.4"),sQuery(id+"F3.wireOp",EDGE,"E32.2.5"),sQuery(id+"F3.wireOp",EDGE,"E32.2.6"),sQuery(id+"F3.wireOp",EDGE,"E32.2.7"),sQuery(id+"F3.wireOp",EDGE,"E32.3.0"),sQuery(id+"F3.wireOp",EDGE,"E32.3.1"),sQuery(id+"F3.wireOp",EDGE,"E32.3.2"),sQuery(id+"F3.wireOp",EDGE,"E32.3.3"),sQuery(id+"F3.wireOp",EDGE,"E32.3.4"),sQuery(id+"F3.wireOp",EDGE,"E32.3.5"),sQuery(id+"F3.wireOp",EDGE,"E32.3.6"),sQuery(id+"F3.wireOp",EDGE,"E32.3.7"),sQuery(id+"F3.wireOp",EDGE,"E33.bottom"),sQuery(id+"F3.wireOp",EDGE,"E33.top"),sQuery(id+"F3.wireOp",EDGE,"E33.left"),sQuery(id+"F3.wireOp",EDGE,"E33.right"),sQuery(id+"F3.wireOp",EDGE,"E34.1.0.1"),sQuery(id+"F3.wireOp",EDGE,"E34.1.0.2"),sQuery(id+"F3.wireOp",EDGE,"E34.1.0.3"),sQuery(id+"F3.wireOp",EDGE,"E34.1.0.4"),sQuery(id+"F3.wireOp",EDGE,"E34.2.0.1"),sQuery(id+"F3.wireOp",EDGE,"E34.2.0.2"),sQuery(id+"F3.wireOp",EDGE,"E34.2.0.3"),sQuery(id+"F3.wireOp",EDGE,"E34.2.0.4"),sQuery(id+"F3.wireOp",EDGE,"E34.3.0.1"),sQuery(id+"F3.wireOp",EDGE,"E34.3.0.2"),sQuery(id+"F3.wireOp",EDGE,"E34.3.0.3"),sQuery(id+"F3.wireOp",EDGE,"E34.3.0.4")])]});
            var Q1;
            Q1=qCreatedBy(makeId("Top.planeOp"),FACE);
            transform(context, id + "F7", {"entities" : qUnion([Q0]), "transformType" : TransformType.TRANSLATION_DISTANCE, "transformDirection" : qUnion([Q1]), "distance" : .1 * mm, "makeCopy" : false});
        }
        {
            var Q0;
            Q0=makeQuery(id+"F1.opExtrude","CAP_FACE",FACE,{"disambiguationData":[OSD([sQuery(id+"FUyg42RqR56omhc_0.wireOp",EDGE,"apNCEg5n-BcgS-b9KA-570i-48yKU28l5lF8"),sQuery(id+"F0.wireOp",EDGE,"E0.bottom"),sQuery(id+"F0.wireOp",EDGE,"E0.top"),sQuery(id+"F0.wireOp",EDGE,"E0.left"),sQuery(id+"F0.wireOp",EDGE,"E0.right"),sQuery(id+"F0.wireOp",EDGE,"E1.filletArc"),sQuery(id+"F0.wireOp",EDGE,"E2.filletArc"),sQuery(id+"F0.wireOp",EDGE,"E3.filletArc"),sQuery(id+"F0.wireOp",EDGE,"E4.filletArc"),sQuery(id+"F0.wireOp",EDGE,"E6"),sQuery(id+"F0.wireOp",EDGE,"E8.trimOffspring"),sQuery(id+"F0.wireOp",EDGE,"E10.left"),sQuery(id+"F0.wireOp",EDGE,"E10.right"),sQuery(id+"F0.wireOp",EDGE,"E11"),sQuery(id+"F0.wireOp",EDGE,"E12"),sQuery(id+"F0.wireOp",EDGE,"E13.MirrorCS"),sQuery(id+"F0.wireOp",EDGE,"E14.MirrorCS"),sQuery(id+"F0.wireOp",EDGE,"E16.MirrorCS"),sQuery(id+"F0.wireOp",EDGE,"E17.MirrorCS")])],"isStart":false});
            var sketch = newSketch(context, id + "F8", { "sketchPlane" : qUnion([Q0])});
            skArc(sketch, "E51.0", {"start": v(-14.5, 18.75) * mm, "mid": v(-17.5, 17.5) * mm, "end": v(-18.75, 14.5) * mm});
            skLineSegment(sketch, "E51.1", {"start": v(14.5, 18.75) * mm, "end": v(-14.5, 18.75) * mm});
            skArc(sketch, "E51.2", {"start": v(18.75, 14.5) * mm, "mid": v(17.5, 17.5) * mm, "end": v(14.5, 18.75) * mm});
            skLineSegment(sketch, "E51.3", {"start": v(18.75, -14.5) * mm, "end": v(18.75, 14.5) * mm});
            skArc(sketch, "E51.4", {"start": v(14.5, -18.75) * mm, "mid": v(17.5, -17.5) * mm, "end": v(18.75, -14.5) * mm});
            skLineSegment(sketch, "E51.5", {"start": v(14.5, -18.75) * mm, "end": v(-14.5, -18.75) * mm});
            skArc(sketch, "E51.6", {"start": v(-18.75, -14.5) * mm, "mid": v(-17.5, -17.5) * mm, "end": v(-14.5, -18.75) * mm});
            skLineSegment(sketch, "E51.7", {"start": v(-18.75, -14.5) * mm, "end": v(-18.75, 14.5) * mm});
            skCircle(sketch, "E51.8", {"center": v(-15.05, -15.05) * mm, "radius": 2.3 * mm});
            skCircle(sketch, "E51.9", {"center": v(-15.05, 15.05) * mm, "radius": 2.3 * mm});
            skCircle(sketch, "E51.10", {"center": v(15.05, 15.05) * mm, "radius": 2.3 * mm});
            skCircle(sketch, "E51.11", {"center": v(15.05, -15.05) * mm, "radius": 2.3 * mm});
            skArc(sketch, "E51.12", {"start": v(17.2, -7) * mm, "mid": v(15.5, -8.7) * mm, "end": v(13.8, -7) * mm});
            skLineSegment(sketch, "E51.13", {"start": v(13.8, 7) * mm, "end": v(13.8, -7) * mm});
            skLineSegment(sketch, "E51.14", {"start": v(17.2, 7) * mm, "end": v(17.2, -7) * mm});
            skArc(sketch, "E51.15", {"start": v(13.8, 7) * mm, "mid": v(15.5, 8.7) * mm, "end": v(17.2, 7) * mm});
            skArc(sketch, "E51.16", {"start": v(-13.8, 7) * mm, "mid": v(-15.5, 8.7) * mm, "end": v(-17.2, 7) * mm});
            skLineSegment(sketch, "E51.17", {"start": v(-13.8, 7) * mm, "end": v(-13.8, -7) * mm});
            skLineSegment(sketch, "E51.18", {"start": v(-17.2, 7) * mm, "end": v(-17.2, -7) * mm});
            skArc(sketch, "E51.19", {"start": v(-17.2, -7) * mm, "mid": v(-15.5, -8.7) * mm, "end": v(-13.8, -7) * mm});
            skSolve(sketch);
        }
        {
            var Q0;
            Q0=qSketchRegion(id+"F8",true);
            extrude(context, id + "F9", {"entities" : qUnion([Q0]), "depth" : .1 * mm});
        }
        {
            var Q0;
            Q0=makeQuery(id+"F9.opExtrude","CAP_FACE",FACE,{"disambiguationData":[OSD([sQuery(id+"F8.wireOp",EDGE,"E51.0"),sQuery(id+"F8.wireOp",EDGE,"E51.1"),sQuery(id+"F8.wireOp",EDGE,"E51.2"),sQuery(id+"F8.wireOp",EDGE,"E51.3"),sQuery(id+"F8.wireOp",EDGE,"E51.4"),sQuery(id+"F8.wireOp",EDGE,"E51.5"),sQuery(id+"F8.wireOp",EDGE,"E51.6"),sQuery(id+"F8.wireOp",EDGE,"E51.7"),sQuery(id+"F8.wireOp",EDGE,"E51.8"),sQuery(id+"F8.wireOp",EDGE,"E51.9"),sQuery(id+"F8.wireOp",EDGE,"E51.10"),sQuery(id+"F8.wireOp",EDGE,"E51.11"),sQuery(id+"F8.wireOp",EDGE,"E51.12"),sQuery(id+"F8.wireOp",EDGE,"E51.13"),sQuery(id+"F8.wireOp",EDGE,"E51.14"),sQuery(id+"F8.wireOp",EDGE,"E51.15"),sQuery(id+"F8.wireOp",EDGE,"E51.16"),sQuery(id+"F8.wireOp",EDGE,"E51.17"),sQuery(id+"F8.wireOp",EDGE,"E51.18"),sQuery(id+"F8.wireOp",EDGE,"E51.19")])],"isStart":false});
            var sketch = newSketch(context, id + "F10", { "sketchPlane" : qUnion([Q0])});
            skLineSegment(sketch, "E52.0", {"start": v(14.5, 19.5) * mm, "end": v(-14.5, 19.5) * mm});
            skArc(sketch, "E52.1", {"start": v(-14.5, 19.5) * mm, "mid": v(-18.04, 18.04) * mm, "end": v(-19.5, 14.5) * mm});
            skLineSegment(sketch, "E52.2", {"start": v(-19.5, -14.5) * mm, "end": v(-19.5, 14.5) * mm});
            skArc(sketch, "E52.3", {"start": v(-19.5, -14.5) * mm, "mid": v(-18.04, -18.04) * mm, "end": v(-14.5, -19.5) * mm});
            skLineSegment(sketch, "E52.4", {"start": v(14.5, -19.5) * mm, "end": v(-14.5, -19.5) * mm});
            skArc(sketch, "E52.5", {"start": v(14.5, -19.5) * mm, "mid": v(18.04, -18.04) * mm, "end": v(19.5, -14.5) * mm});
            skLineSegment(sketch, "E52.6", {"start": v(19.5, -14.5) * mm, "end": v(19.5, 14.5) * mm});
            skArc(sketch, "E52.7", {"start": v(19.5, 14.5) * mm, "mid": v(18.04, 18.04) * mm, "end": v(14.5, 19.5) * mm});
            skCircle(sketch, "E53.0", {"center": v(-15.05, 15.05) * mm, "radius": 1.55 * mm});
            skCircle(sketch, "E53.1", {"center": v(15.05, 15.05) * mm, "radius": 1.55 * mm});
            skCircle(sketch, "E53.2", {"center": v(-15.05, -15.05) * mm, "radius": 1.55 * mm});
            skLineSegment(sketch, "E54.0", {"start": v(-14.5, 7) * mm, "end": v(-14.5, -7) * mm});
            skArc(sketch, "E54.1", {"start": v(-14.5, 7) * mm, "mid": v(-15.5, 8) * mm, "end": v(-16.5, 7) * mm});
            skLineSegment(sketch, "E54.2", {"start": v(-16.5, 7) * mm, "end": v(-16.5, -7) * mm});
            skArc(sketch, "E54.3", {"start": v(-16.5, -7) * mm, "mid": v(-15.5, -8) * mm, "end": v(-14.5, -7) * mm});
            skArc(sketch, "E54.4", {"start": v(14.5, 7) * mm, "mid": v(15.5, 8) * mm, "end": v(16.5, 7) * mm});
            skLineSegment(sketch, "E54.5", {"start": v(16.5, 7) * mm, "end": v(16.5, -7) * mm});
            skLineSegment(sketch, "E54.6", {"start": v(14.5, 7) * mm, "end": v(14.5, -7) * mm});
            skArc(sketch, "E54.7", {"start": v(16.5, -7) * mm, "mid": v(15.5, -8) * mm, "end": v(14.5, -7) * mm});
            skCircle(sketch, "E55.0", {"center": v(15.05, -15.05) * mm, "radius": 1.55 * mm});
            skSolve(sketch);
        }
        {
            var Q0;
            Q0=qSketchRegion(id+"F10",true);
            extrude(context, id + "F11", {"entities" : qUnion([Q0]), "depth" : .1 * mm});
        }
        {
            var Q0;
            Q0=makeQuery(id+"F11.opExtrude","CAP_FACE",FACE,{"disambiguationData":[OSD([sQuery(id+"F10.wireOp",EDGE,"E52.0"),sQuery(id+"F10.wireOp",EDGE,"E52.1"),sQuery(id+"F10.wireOp",EDGE,"E52.2"),sQuery(id+"F10.wireOp",EDGE,"E52.3"),sQuery(id+"F10.wireOp",EDGE,"E52.4"),sQuery(id+"F10.wireOp",EDGE,"E52.5"),sQuery(id+"F10.wireOp",EDGE,"E52.6"),sQuery(id+"F10.wireOp",EDGE,"E52.7"),sQuery(id+"F10.wireOp",EDGE,"E53.0"),sQuery(id+"F10.wireOp",EDGE,"E53.1"),sQuery(id+"F10.wireOp",EDGE,"E53.2"),sQuery(id+"F10.wireOp",EDGE,"E54.0"),sQuery(id+"F10.wireOp",EDGE,"E54.1"),sQuery(id+"F10.wireOp",EDGE,"E54.2"),sQuery(id+"F10.wireOp",EDGE,"E54.3"),sQuery(id+"F10.wireOp",EDGE,"E54.4"),sQuery(id+"F10.wireOp",EDGE,"E54.5"),sQuery(id+"F10.wireOp",EDGE,"E54.6"),sQuery(id+"F10.wireOp",EDGE,"E54.7")])],"isStart":false});
            var sketch = newSketch(context, id + "F12", { "sketchPlane" : qUnion([Q0])});
            skLineSegment(sketch, "E56.1.0", {"start": v(2.17, 1.56) * mm, "end": v(2.17, -1.95) * mm});
            skLineSegment(sketch, "E56.1.1", {"start": v(0.69, -12.32) * mm, "end": v(4.17, -12.93) * mm});
            skLineSegment(sketch, "E56.1.2", {"start": v(2.52, 4.09) * mm, "end": v(-0.81, 4.67) * mm});
            skPoint(sketch, "E56.1.3", {"position": v(2.17, 11.6) * mm});
            skPoint(sketch, "E56.1.4", {"position": v(1.55, 7.64) * mm});
            skPoint(sketch, "E56.1.5", {"position": v(2.17, 2.12) * mm});
            skLineSegment(sketch, "E56.1.6", {"start": v(4.17, -11) * mm, "end": v(0.69, -12.32) * mm});
            skPoint(sketch, "E56.1.7", {"position": v(3.14, -6.16) * mm});
            skLineSegment(sketch, "E56.1.8", {"start": v(4.17, -2.3) * mm, "end": v(4.17, 2.12) * mm});
            skPoint(sketch, "E56.1.9", {"position": v(-3.16, 5.09) * mm});
            skPoint(sketch, "E56.1.10", {"position": v(-3.16, 8.47) * mm});
            skLineSegment(sketch, "E56.1.11", {"start": v(0.32, -10.32) * mm, "end": v(-3.16, -9.7) * mm});
            skLineSegment(sketch, "E56.1.12", {"start": v(-3.16, 10.15) * mm, "end": v(-3.16, 14.56) * mm});
            skLineSegment(sketch, "E56.1.13", {"start": v(4.17, 7.18) * mm, "end": v(4.17, 11.6) * mm});
            skLineSegment(sketch, "E56.1.14", {"start": v(-3.16, -11.64) * mm, "end": v(0.32, -10.32) * mm});
            skLineSegment(sketch, "E56.1.15", {"start": v(4.17, -8.32) * mm, "end": v(-3.16, -7.34) * mm});
            skLineSegment(sketch, "E56.1.16", {"start": v(4.17, -8.96) * mm, "end": v(-3.16, -7.67) * mm});
            skLineSegment(sketch, "E56.1.17", {"start": v(-3.16, 5.76) * mm, "end": v(4.17, 4.47) * mm});
            skPoint(sketch, "E56.1.18", {"position": v(-1.16, 2.7) * mm});
            skPoint(sketch, "E56.1.19", {"position": v(-0.45, 14.09) * mm});
            skPoint(sketch, "E56.1.20", {"position": v(-1.16, 10.15) * mm});
            skPoint(sketch, "E56.1.21", {"position": v(-1.16, 0.67) * mm});
            skPoint(sketch, "E56.1.22", {"position": v(4.17, 3.8) * mm});
            skPoint(sketch, "E56.1.23", {"position": v(4.17, 13.27) * mm});
            skLineSegment(sketch, "E56.1.24", {"start": v(-3.16, -1.34) * mm, "end": v(4.17, -4.47) * mm});
            skLineSegment(sketch, "E56.1.25", {"start": v(4.17, -14.96) * mm, "end": v(-3.16, -13.67) * mm});
            skLineSegment(sketch, "E56.1.26", {"start": v(-3.16, -1) * mm, "end": v(1.65, -1.85) * mm});
            skPoint(sketch, "E56.1.27", {"position": v(-0.45, 10.03) * mm});
            skPoint(sketch, "E56.1.28", {"position": v(-3.16, -1) * mm});
            skLineSegment(sketch, "E56.1.29", {"start": v(-3.16, 2.7) * mm, "end": v(-3.16, -1) * mm});
            skPoint(sketch, "E56.1.30", {"position": v(-0.35, 0.53) * mm});
            skLineSegment(sketch, "E56.1.31", {"start": v(4.17, -4.47) * mm, "end": v(4.17, -8.32) * mm});
            skLineSegment(sketch, "E56.1.32", {"start": v(1.65, -1.85) * mm, "end": v(1.65, 1.13) * mm});
            skPoint(sketch, "E56.1.33", {"position": v(-3.16, 5.09) * mm});
            skPoint(sketch, "E56.1.34", {"position": v(1.55, 11.7) * mm});
            skLineSegment(sketch, "E56.1.35", {"start": v(-2, -5.47) * mm, "end": v(-2, -3.96) * mm});
            skArc(sketch, "E56.1.36", {"start": v(4.17, 2.12) * mm, "mid": v(3.7, 3.4) * mm, "end": v(2.52, 4.09) * mm});
            skArc(sketch, "E56.1.37", {"start": v(-0.02, 7.92) * mm, "mid": v(1.07, 8.2) * mm, "end": v(1.55, 9.23) * mm});
            skLineSegment(sketch, "E56.1.38", {"start": v(-3.16, -5.32) * mm, "end": v(-2, -5.47) * mm});
            skLineSegment(sketch, "E56.1.39", {"start": v(-3.16, -9.7) * mm, "end": v(-3.16, -7.67) * mm});
            skLineSegment(sketch, "E56.1.40", {"start": v(4.17, -8.96) * mm, "end": v(4.17, -11) * mm});
            skLineSegment(sketch, "E56.1.41", {"start": v(4.17, 4.47) * mm, "end": v(4.17, 6.5) * mm});
            skLineSegment(sketch, "E56.1.42", {"start": v(-3.16, -7.34) * mm, "end": v(-3.16, -5.32) * mm});
            skArc(sketch, "E56.1.43", {"start": v(4.17, 11.6) * mm, "mid": v(3.7, 12.88) * mm, "end": v(2.52, 13.56) * mm});
            skLineSegment(sketch, "E56.1.44", {"start": v(-1.16, 14.21) * mm, "end": v(-1.16, 10.37) * mm});
            skLineSegment(sketch, "E56.1.45", {"start": v(-3.16, 14.56) * mm, "end": v(-1.16, 14.21) * mm});
            skLineSegment(sketch, "E56.1.46", {"start": v(1.55, 11.39) * mm, "end": v(1.55, 9.23) * mm});
            skLineSegment(sketch, "E56.1.47", {"start": v(2.17, 7.53) * mm, "end": v(2.17, 11.37) * mm});
            skLineSegment(sketch, "E56.1.48", {"start": v(4.17, 7.18) * mm, "end": v(2.17, 7.53) * mm});
            skArc(sketch, "E56.1.49", {"start": v(-3.16, 10.15) * mm, "mid": v(-2.7, 8.86) * mm, "end": v(-1.5, 8.18) * mm});
            skLineSegment(sketch, "E56.1.50", {"start": v(-0.34, -5.7) * mm, "end": v(1.71, -5.97) * mm});
            skLineSegment(sketch, "E56.1.51", {"start": v(-3.16, -13.67) * mm, "end": v(-3.16, -11.64) * mm});
            skArc(sketch, "E56.1.52", {"start": v(-0.81, 4.67) * mm, "mid": v(-2.45, 4.24) * mm, "end": v(-3.16, 2.7) * mm});
            skLineSegment(sketch, "E56.1.53", {"start": v(1.82, -5.6) * mm, "end": v(-0.34, -4.67) * mm});
            skLineSegment(sketch, "E56.1.54", {"start": v(-0.34, -4.67) * mm, "end": v(-0.34, -5.7) * mm});
            skLineSegment(sketch, "E56.1.55", {"start": v(4.17, 6.5) * mm, "end": v(-3.16, 7.8) * mm});
            skLineSegment(sketch, "E56.1.56", {"start": v(-3.16, -3.47) * mm, "end": v(-3.16, -1.34) * mm});
            skLineSegment(sketch, "E56.1.57", {"start": v(2.17, -1.95) * mm, "end": v(4.17, -2.3) * mm});
            skLineSegment(sketch, "E56.1.58", {"start": v(4.17, -12.93) * mm, "end": v(4.17, -14.96) * mm});
            skLineSegment(sketch, "E56.1.59", {"start": v(-2, -3.96) * mm, "end": v(-3.16, -3.47) * mm});
            skArc(sketch, "E56.1.60", {"start": v(1.11, 13.81) * mm, "mid": v(0.03, 13.52) * mm, "end": v(-0.45, 12.5) * mm});
            skLineSegment(sketch, "E56.1.61", {"start": v(1.11, 13.81) * mm, "end": v(2.52, 13.56) * mm});
            skLineSegment(sketch, "E56.1.62", {"start": v(-0.45, 10.34) * mm, "end": v(-0.45, 12.5) * mm});
            skLineSegment(sketch, "E56.1.63", {"start": v(-0.02, 7.92) * mm, "end": v(-1.5, 8.18) * mm});
            skLineSegment(sketch, "E56.1.64", {"start": v(-3.16, 7.8) * mm, "end": v(-3.16, 5.76) * mm});
            skArc(sketch, "E56.1.65", {"start": v(1.71, -5.97) * mm, "mid": v(1.93, -5.83) * mm, "end": v(1.82, -5.6) * mm});
            skLineSegment(sketch, "E56.1.66", {"start": v(-0.38, 2.57) * mm, "end": v(1.62, 2.21) * mm});
            skLineSegment(sketch, "E56.1.67", {"start": v(1.65, 1.13) * mm, "end": v(-0.35, 1.48) * mm});
            skArc(sketch, "E56.1.68", {"start": v(2.17, 1.56) * mm, "mid": v(2.02, 1.99) * mm, "end": v(1.62, 2.21) * mm});
            skLineSegment(sketch, "E56.1.69", {"start": v(-1.16, 0.67) * mm, "end": v(-1.16, 1.9) * mm});
            skLineSegment(sketch, "E56.1.70", {"start": v(-0.74, 0.6) * mm, "end": v(-1.16, 0.67) * mm});
            skLineSegment(sketch, "E56.1.71", {"start": v(-0.35, 1.48) * mm, "end": v(-0.35, 0.93) * mm});
            skArc(sketch, "E56.1.72", {"start": v(-0.38, 2.57) * mm, "mid": v(-0.92, 2.42) * mm, "end": v(-1.16, 1.9) * mm});
            skArc(sketch, "E56.1.73", {"start": v(-0.74, 0.6) * mm, "mid": v(-0.47, 0.67) * mm, "end": v(-0.35, 0.93) * mm});
            skArc(sketch, "E56.1.74", {"start": v(-0.76, 10.08) * mm, "mid": v(-0.55, 10.14) * mm, "end": v(-0.45, 10.34) * mm});
            skLineSegment(sketch, "E56.1.75", {"start": v(-0.94, 10.11) * mm, "end": v(-0.76, 10.08) * mm});
            skLineSegment(sketch, "E56.1.76", {"start": v(1.95, 11.63) * mm, "end": v(1.86, 11.65) * mm});
            skArc(sketch, "E56.1.77", {"start": v(1.86, 11.65) * mm, "mid": v(1.64, 11.59) * mm, "end": v(1.55, 11.39) * mm});
            skArc(sketch, "E56.1.78", {"start": v(2.17, 11.37) * mm, "mid": v(2.1, 11.54) * mm, "end": v(1.95, 11.63) * mm});
            skArc(sketch, "E56.1.79", {"start": v(-1.16, 10.37) * mm, "mid": v(-1.1, 10.2) * mm, "end": v(-0.94, 10.11) * mm});
            skLineSegment(sketch, "E57.0", {"start": v(14.5, 19.5) * mm, "end": v(-14.5, 19.5) * mm});
            skArc(sketch, "E57.1", {"start": v(-14.5, 19.5) * mm, "mid": v(-18.04, 18.04) * mm, "end": v(-19.5, 14.5) * mm});
            skLineSegment(sketch, "E57.2", {"start": v(-19.5, -14.5) * mm, "end": v(-19.5, 14.5) * mm});
            skArc(sketch, "E57.3", {"start": v(-19.5, -14.5) * mm, "mid": v(-18.04, -18.04) * mm, "end": v(-14.5, -19.5) * mm});
            skLineSegment(sketch, "E57.4", {"start": v(14.5, -19.5) * mm, "end": v(-14.5, -19.5) * mm});
            skArc(sketch, "E57.5", {"start": v(14.5, -19.5) * mm, "mid": v(18.04, -18.04) * mm, "end": v(19.5, -14.5) * mm});
            skLineSegment(sketch, "E57.6", {"start": v(19.5, -14.5) * mm, "end": v(19.5, 14.5) * mm});
            skArc(sketch, "E57.7", {"start": v(19.5, 14.5) * mm, "mid": v(18.04, 18.04) * mm, "end": v(14.5, 19.5) * mm});
            skSolve(sketch);
        }
        {
            var Q0;
            Q0=makeQuery(id+"F12.imprint","IMPRINT",FACE,{"disambiguationData":[TD([[makeQuery(id+"F12.imprint","IMPRINT",EDGE,{"derivedFrom":sQuery(id+"F12.wireOp",EDGE,"E56.1.0")}),-1.0]])]});
            var Q1;
            Q1=makeQuery(id+"F12.imprint","IMPRINT",FACE,{"disambiguationData":[TD([[makeQuery(id+"F12.imprint","IMPRINT",EDGE,{"derivedFrom":sQuery(id+"F12.wireOp",EDGE,"E56.1.50")}),1.0]])]});
            extrude(context, id + "F13", {"entities" : qUnion([Q0, Q1]), "depth" : .1 * mm});
        }
        {
            var Q0;
            Q0=makeQuery(id+"F4.opExtrude","CAP_FACE",FACE,{"disambiguationData":[OSD([sQuery(id+"FUyg42RqR56omhc_0.wireOp",EDGE,"apNCEg5n-BcgS-b9KA-570i-48yKU28l5lF8"),sQuery(id+"F0.wireOp",EDGE,"E0.bottom"),sQuery(id+"F0.wireOp",EDGE,"E0.top"),sQuery(id+"F0.wireOp",EDGE,"E0.left"),sQuery(id+"F0.wireOp",EDGE,"E0.right"),sQuery(id+"F0.wireOp",EDGE,"E1.filletArc"),sQuery(id+"F0.wireOp",EDGE,"E2.filletArc"),sQuery(id+"F0.wireOp",EDGE,"E3.filletArc"),sQuery(id+"F0.wireOp",EDGE,"E4.filletArc"),sQuery(id+"F0.wireOp",EDGE,"E5"),sQuery(id+"F0.wireOp",EDGE,"E6"),sQuery(id+"F0.wireOp",EDGE,"E7"),sQuery(id+"F0.wireOp",EDGE,"E8.trimOffspring"),sQuery(id+"F0.wireOp",EDGE,"E10.left"),sQuery(id+"F0.wireOp",EDGE,"E10.right"),sQuery(id+"F0.wireOp",EDGE,"E11"),sQuery(id+"F0.wireOp",EDGE,"E12"),sQuery(id+"F0.wireOp",EDGE,"E13.MirrorCS"),sQuery(id+"F0.wireOp",EDGE,"E14.MirrorCS"),sQuery(id+"F0.wireOp",EDGE,"E16.MirrorCS"),sQuery(id+"F0.wireOp",EDGE,"E17.MirrorCS"),sQuery(id+"F3.wireOp",EDGE,"E19.bottom"),sQuery(id+"F3.wireOp",EDGE,"E19.top"),sQuery(id+"F3.wireOp",EDGE,"E19.left"),sQuery(id+"F3.wireOp",EDGE,"E19.right"),sQuery(id+"F3.wireOp",EDGE,"E20.1.0.0"),sQuery(id+"F3.wireOp",EDGE,"E20.1.0.1"),sQuery(id+"F3.wireOp",EDGE,"E20.1.0.2"),sQuery(id+"F3.wireOp",EDGE,"E20.1.0.3"),sQuery(id+"F3.wireOp",EDGE,"E21"),sQuery(id+"F3.wireOp",EDGE,"E22"),sQuery(id+"F3.wireOp",EDGE,"E23"),sQuery(id+"F3.wireOp",EDGE,"E24"),sQuery(id+"F3.wireOp",EDGE,"E28.MirrorCS"),sQuery(id+"F3.wireOp",EDGE,"E29.MirrorCS"),sQuery(id+"F3.wireOp",EDGE,"E30.MirrorCS"),sQuery(id+"F3.wireOp",EDGE,"E31.MirrorCS"),sQuery(id+"F3.wireOp",EDGE,"E32.1.0"),sQuery(id+"F3.wireOp",EDGE,"E32.1.1"),sQuery(id+"F3.wireOp",EDGE,"E32.1.2"),sQuery(id+"F3.wireOp",EDGE,"E32.1.3"),sQuery(id+"F3.wireOp",EDGE,"E32.1.4"),sQuery(id+"F3.wireOp",EDGE,"E32.1.5"),sQuery(id+"F3.wireOp",EDGE,"E32.1.6"),sQuery(id+"F3.wireOp",EDGE,"E32.1.7"),sQuery(id+"F3.wireOp",EDGE,"E32.2.0"),sQuery(id+"F3.wireOp",EDGE,"E32.2.1"),sQuery(id+"F3.wireOp",EDGE,"E32.2.2"),sQuery(id+"F3.wireOp",EDGE,"E32.2.3"),sQuery(id+"F3.wireOp",EDGE,"E32.2.4"),sQuery(id+"F3.wireOp",EDGE,"E32.2.5"),sQuery(id+"F3.wireOp",EDGE,"E32.2.6"),sQuery(id+"F3.wireOp",EDGE,"E32.2.7"),sQuery(id+"F3.wireOp",EDGE,"E32.3.0"),sQuery(id+"F3.wireOp",EDGE,"E32.3.1"),sQuery(id+"F3.wireOp",EDGE,"E32.3.2"),sQuery(id+"F3.wireOp",EDGE,"E32.3.3"),sQuery(id+"F3.wireOp",EDGE,"E32.3.4"),sQuery(id+"F3.wireOp",EDGE,"E32.3.5"),sQuery(id+"F3.wireOp",EDGE,"E32.3.6"),sQuery(id+"F3.wireOp",EDGE,"E32.3.7"),sQuery(id+"F3.wireOp",EDGE,"E33.bottom"),sQuery(id+"F3.wireOp",EDGE,"E33.top"),sQuery(id+"F3.wireOp",EDGE,"E33.left"),sQuery(id+"F3.wireOp",EDGE,"E33.right"),sQuery(id+"F3.wireOp",EDGE,"E34.1.0.1"),sQuery(id+"F3.wireOp",EDGE,"E34.1.0.2"),sQuery(id+"F3.wireOp",EDGE,"E34.1.0.3"),sQuery(id+"F3.wireOp",EDGE,"E34.1.0.4"),sQuery(id+"F3.wireOp",EDGE,"E34.2.0.1"),sQuery(id+"F3.wireOp",EDGE,"E34.2.0.2"),sQuery(id+"F3.wireOp",EDGE,"E34.2.0.3"),sQuery(id+"F3.wireOp",EDGE,"E34.2.0.4"),sQuery(id+"F3.wireOp",EDGE,"E34.3.0.1"),sQuery(id+"F3.wireOp",EDGE,"E34.3.0.2"),sQuery(id+"F3.wireOp",EDGE,"E34.3.0.3"),sQuery(id+"F3.wireOp",EDGE,"E34.3.0.4")])],"isStart":false});
            var sketch = newSketch(context, id + "F14", { "sketchPlane" : qUnion([Q0])});
            skLineSegment(sketch, "E58.0", {"start": v(7.5, -19.5) * mm, "end": v(7.5, -19.5) * mm});
            skLineSegment(sketch, "E58.1", {"start": v(7.5, -19.5) * mm, "end": v(14.5, -19.5) * mm});
            skLineSegment(sketch, "E58.2", {"start": v(14.5, -19.5) * mm, "end": v(7.5, -19.5) * mm});
            skArc(sketch, "E58.3", {"start": v(19.5, -14.5) * mm, "mid": v(18.04, -18.04) * mm, "end": v(14.5, -19.5) * mm});
            skLineSegment(sketch, "E58.4", {"start": v(19.5, 14.5) * mm, "end": v(19.5, -14.5) * mm});
            skArc(sketch, "E58.5", {"start": v(14.5, 19.5) * mm, "mid": v(18.04, 18.04) * mm, "end": v(19.5, 14.5) * mm});
            skLineSegment(sketch, "E58.6", {"start": v(14.5, 19.5) * mm, "end": v(-14.5, 19.5) * mm});
            skArc(sketch, "E58.7", {"start": v(-19.5, 14.5) * mm, "mid": v(-18.04, 18.04) * mm, "end": v(-14.5, 19.5) * mm});
            skLineSegment(sketch, "E58.8", {"start": v(-19.5, 14.5) * mm, "end": v(-19.5, -14.5) * mm});
            skArc(sketch, "E58.9", {"start": v(-14.5, -19.5) * mm, "mid": v(-18.04, -18.04) * mm, "end": v(-19.5, -14.5) * mm});
            skPoint(sketch, "E59.center", {"position": v(0, 0) * mm});
            skLineSegment(sketch, "E60.bottom", {"start": v(2.35, 12.93) * mm, "end": v(2.63, 12.93) * mm});
            skLineSegment(sketch, "E60.top", {"start": v(2.35, 11.9) * mm, "end": v(2.63, 11.9) * mm});
            skLineSegment(sketch, "E60.left", {"start": v(2.35, 12.93) * mm, "end": v(2.35, 12.55) * mm});
            skLineSegment(sketch, "E60.right", {"start": v(2.63, 12.93) * mm, "end": v(2.63, 12.55) * mm});
            skPoint(sketch, "E60.middle", {"position": v(2.5, 12.41) * mm});
            skLineSegment(sketch, "E61.bottom", {"start": v(3, 12.27) * mm, "end": v(2.63, 12.27) * mm});
            skLineSegment(sketch, "E61.top", {"start": v(3, 12.55) * mm, "end": v(2.63, 12.55) * mm});
            skLineSegment(sketch, "E61.left", {"start": v(3, 12.27) * mm, "end": v(3, 12.55) * mm});
            skLineSegment(sketch, "E61.right", {"start": v(1.98, 12.27) * mm, "end": v(1.98, 12.55) * mm});
            skLineSegment(sketch, "E62.bottom", {"start": v(-1.98, 12.27) * mm, "end": v(-3, 12.27) * mm});
            skLineSegment(sketch, "E62.top", {"start": v(-1.98, 12.55) * mm, "end": v(-3, 12.55) * mm});
            skLineSegment(sketch, "E62.left", {"start": v(-1.98, 12.27) * mm, "end": v(-1.98, 12.55) * mm});
            skLineSegment(sketch, "E62.right", {"start": v(-3, 12.27) * mm, "end": v(-3, 12.55) * mm});
            skPoint(sketch, "E62.middle", {"position": v(-2.5, 12.41) * mm});
            skPoint(sketch, "E62.middle.positionSnap0", {"position": v(1.98, 12.41) * mm});
            skPoint(sketch, "E62.centerSnap0", {"position": v(1.98, 12.41) * mm});
            skLineSegment(sketch, "E63.bottom", {"start": v(3.47, -12.47) * mm, "end": v(2.77, -12.47) * mm});
            skLineSegment(sketch, "E63.top", {"start": v(3.47, -9.84) * mm, "end": v(2.77, -9.84) * mm});
            skLineSegment(sketch, "E63.left", {"start": v(3.47, -12.47) * mm, "end": v(3.47, -11.5) * mm});
            skLineSegment(sketch, "E63.right", {"start": v(2.77, -12.47) * mm, "end": v(2.77, -11.5) * mm});
            skPoint(sketch, "E63.middle", {"position": v(3.12, -11.15) * mm});
            skLineSegment(sketch, "E64.bottom", {"start": v(4.44, -11.5) * mm, "end": v(3.47, -11.5) * mm});
            skLineSegment(sketch, "E64.top", {"start": v(4.44, -10.8) * mm, "end": v(3.47, -10.8) * mm});
            skLineSegment(sketch, "E64.left", {"start": v(4.44, -11.5) * mm, "end": v(4.44, -10.8) * mm});
            skLineSegment(sketch, "E64.right", {"start": v(1.8, -11.5) * mm, "end": v(1.8, -10.8) * mm});
            skLineSegment(sketch, "E65.bottom", {"start": v(-3.1, -11.5) * mm, "end": v(-5.72, -11.5) * mm});
            skLineSegment(sketch, "E65.top", {"start": v(-3.1, -10.8) * mm, "end": v(-5.72, -10.8) * mm});
            skLineSegment(sketch, "E65.left", {"start": v(-3.1, -11.5) * mm, "end": v(-3.1, -10.8) * mm});
            skLineSegment(sketch, "E65.right", {"start": v(-5.72, -11.5) * mm, "end": v(-5.72, -10.8) * mm});
            skPoint(sketch, "E65.middle", {"position": v(-4.4, -11.15) * mm});
            skPoint(sketch, "E65.middle.positionSnap0", {"position": v(1.8, -11.15) * mm});
            skPoint(sketch, "E65.middle.positionSnap1", {"position": v(-4.4, -13.8) * mm});
            skPoint(sketch, "E65.centerSnap0", {"position": v(1.8, -11.15) * mm});
            skPoint(sketch, "E65.centerSnap1", {"position": v(-4.4, -13.8) * mm});
            skLineSegment(sketch, "E66.trimOffspring", {"start": v(2.35, 12.55) * mm, "end": v(1.98, 12.55) * mm});
            skLineSegment(sketch, "E67.trimOffspring", {"start": v(2.63, 12.27) * mm, "end": v(2.63, 11.9) * mm});
            skLineSegment(sketch, "E68.trimOffspring", {"start": v(2.35, 12.27) * mm, "end": v(1.98, 12.27) * mm});
            skLineSegment(sketch, "E69.trimOffspring", {"start": v(2.35, 12.27) * mm, "end": v(2.35, 11.9) * mm});
            skLineSegment(sketch, "E70.trimOffspring", {"start": v(2.77, -11.5) * mm, "end": v(1.8, -11.5) * mm});
            skLineSegment(sketch, "E71.trimOffspring", {"start": v(2.77, -10.8) * mm, "end": v(2.77, -9.84) * mm});
            skLineSegment(sketch, "E72.trimOffspring", {"start": v(2.77, -10.8) * mm, "end": v(1.8, -10.8) * mm});
            skLineSegment(sketch, "E73.trimOffspring", {"start": v(3.47, -10.8) * mm, "end": v(3.47, -9.84) * mm});
            skLineSegment(sketch, "E74.bottom", {"start": v(8.36, -11.29) * mm, "end": v(7.66, -11.29) * mm});
            skLineSegment(sketch, "E74.top", {"start": v(8.36, -9.29) * mm, "end": v(7.66, -9.29) * mm});
            skLineSegment(sketch, "E74.left", {"start": v(8.36, -11.29) * mm, "end": v(8.36, -10.64) * mm});
            skLineSegment(sketch, "E74.right", {"start": v(7.66, -11.29) * mm, "end": v(7.66, -10.64) * mm});
            skPoint(sketch, "E74.middle", {"position": v(8, -10.29) * mm});
            skLineSegment(sketch, "E75.bottom", {"start": v(9, -10.64) * mm, "end": v(8.36, -10.64) * mm});
            skLineSegment(sketch, "E75.top", {"start": v(9, -9.94) * mm, "end": v(8.36, -9.94) * mm});
            skLineSegment(sketch, "E75.left", {"start": v(9, -10.64) * mm, "end": v(9, -9.94) * mm});
            skLineSegment(sketch, "E75.right", {"start": v(7, -10.64) * mm, "end": v(7, -9.94) * mm});
            skLineSegment(sketch, "E76.bottom", {"start": v(11.05, -8.53) * mm, "end": v(9.05, -8.53) * mm});
            skLineSegment(sketch, "E76.top", {"start": v(11.05, -7.83) * mm, "end": v(9.05, -7.83) * mm});
            skLineSegment(sketch, "E76.left", {"start": v(11.05, -8.53) * mm, "end": v(11.05, -7.83) * mm});
            skLineSegment(sketch, "E76.right", {"start": v(9.05, -8.53) * mm, "end": v(9.05, -7.83) * mm});
            skLineSegment(sketch, "E77.trimOffspring", {"start": v(7.66, -10.64) * mm, "end": v(7, -10.64) * mm});
            skLineSegment(sketch, "E78.trimOffspring", {"start": v(8.36, -9.94) * mm, "end": v(8.36, -9.29) * mm});
            skLineSegment(sketch, "E79.trimOffspring", {"start": v(7.66, -9.94) * mm, "end": v(7, -9.94) * mm});
            skLineSegment(sketch, "E80.trimOffspring", {"start": v(7.66, -9.94) * mm, "end": v(7.66, -9.29) * mm});
            skLineSegment(sketch, "E81.1.0", {"start": v(-9.94, -8.36) * mm, "end": v(-9.29, -8.36) * mm});
            skLineSegment(sketch, "E81.1.1", {"start": v(-9.29, -8.36) * mm, "end": v(-9.29, -7.66) * mm});
            skLineSegment(sketch, "E81.1.2", {"start": v(-9.94, -7.66) * mm, "end": v(-9.29, -7.66) * mm});
            skLineSegment(sketch, "E81.1.3", {"start": v(-8.53, -11.05) * mm, "end": v(-7.83, -11.05) * mm});
            skLineSegment(sketch, "E81.1.4", {"start": v(-11.29, -8.36) * mm, "end": v(-10.64, -8.36) * mm});
            skLineSegment(sketch, "E81.1.5", {"start": v(-11.29, -8.36) * mm, "end": v(-11.29, -7.66) * mm});
            skPoint(sketch, "E81.1.6", {"position": v(-10.29, -8) * mm});
            skLineSegment(sketch, "E81.1.7", {"start": v(-8.53, -11.05) * mm, "end": v(-8.53, -9.05) * mm});
            skLineSegment(sketch, "E81.1.8", {"start": v(-8.53, -9.05) * mm, "end": v(-7.83, -9.05) * mm});
            skLineSegment(sketch, "E81.1.9", {"start": v(-7.83, -11.05) * mm, "end": v(-7.83, -9.05) * mm});
            skLineSegment(sketch, "E81.1.10", {"start": v(-11.29, -7.66) * mm, "end": v(-10.64, -7.66) * mm});
            skPoint(sketch, "E81.1.11", {"position": v(-10.29, -8) * mm});
            skLineSegment(sketch, "E81.1.12", {"start": v(-9.94, -9) * mm, "end": v(-9.94, -8.36) * mm});
            skLineSegment(sketch, "E81.1.13", {"start": v(-10.64, -9) * mm, "end": v(-9.94, -9) * mm});
            skLineSegment(sketch, "E81.1.14", {"start": v(-10.64, -7) * mm, "end": v(-9.94, -7) * mm});
            skLineSegment(sketch, "E81.1.15", {"start": v(-10.64, -7.66) * mm, "end": v(-10.64, -7) * mm});
            skLineSegment(sketch, "E81.1.16", {"start": v(-9.94, -7.66) * mm, "end": v(-9.94, -7) * mm});
            skLineSegment(sketch, "E81.1.17", {"start": v(-10.64, -9) * mm, "end": v(-10.64, -8.36) * mm});
            skLineSegment(sketch, "E81.2.0", {"start": v(-8.36, 9.94) * mm, "end": v(-8.36, 9.29) * mm});
            skLineSegment(sketch, "E81.2.1", {"start": v(-8.36, 9.29) * mm, "end": v(-7.66, 9.29) * mm});
            skLineSegment(sketch, "E81.2.2", {"start": v(-7.66, 9.94) * mm, "end": v(-7.66, 9.29) * mm});
            skLineSegment(sketch, "E81.2.3", {"start": v(-11.05, 8.53) * mm, "end": v(-11.05, 7.83) * mm});
            skLineSegment(sketch, "E81.2.4", {"start": v(-8.36, 11.29) * mm, "end": v(-8.36, 10.64) * mm});
            skLineSegment(sketch, "E81.2.5", {"start": v(-8.36, 11.29) * mm, "end": v(-7.66, 11.29) * mm});
            skPoint(sketch, "E81.2.6", {"position": v(-8, 10.29) * mm});
            skLineSegment(sketch, "E81.2.7", {"start": v(-11.05, 8.53) * mm, "end": v(-9.05, 8.53) * mm});
            skLineSegment(sketch, "E81.2.8", {"start": v(-9.05, 8.53) * mm, "end": v(-9.05, 7.83) * mm});
            skLineSegment(sketch, "E81.2.9", {"start": v(-11.05, 7.83) * mm, "end": v(-9.05, 7.83) * mm});
            skLineSegment(sketch, "E81.2.10", {"start": v(-7.66, 11.29) * mm, "end": v(-7.66, 10.64) * mm});
            skPoint(sketch, "E81.2.11", {"position": v(-8, 10.29) * mm});
            skLineSegment(sketch, "E81.2.12", {"start": v(-9, 9.94) * mm, "end": v(-8.36, 9.94) * mm});
            skLineSegment(sketch, "E81.2.13", {"start": v(-9, 10.64) * mm, "end": v(-9, 9.94) * mm});
            skLineSegment(sketch, "E81.2.14", {"start": v(-7, 10.64) * mm, "end": v(-7, 9.94) * mm});
            skLineSegment(sketch, "E81.2.15", {"start": v(-7.66, 10.64) * mm, "end": v(-7, 10.64) * mm});
            skLineSegment(sketch, "E81.2.16", {"start": v(-7.66, 9.94) * mm, "end": v(-7, 9.94) * mm});
            skLineSegment(sketch, "E81.2.17", {"start": v(-9, 10.64) * mm, "end": v(-8.36, 10.64) * mm});
            skLineSegment(sketch, "E81.3.0", {"start": v(9.94, 8.36) * mm, "end": v(9.29, 8.36) * mm});
            skLineSegment(sketch, "E81.3.1", {"start": v(9.29, 8.36) * mm, "end": v(9.29, 7.66) * mm});
            skLineSegment(sketch, "E81.3.2", {"start": v(9.94, 7.66) * mm, "end": v(9.29, 7.66) * mm});
            skLineSegment(sketch, "E81.3.3", {"start": v(8.53, 11.05) * mm, "end": v(7.83, 11.05) * mm});
            skLineSegment(sketch, "E81.3.4", {"start": v(11.29, 8.36) * mm, "end": v(10.64, 8.36) * mm});
            skLineSegment(sketch, "E81.3.5", {"start": v(11.29, 8.36) * mm, "end": v(11.29, 7.66) * mm});
            skPoint(sketch, "E81.3.6", {"position": v(10.29, 8) * mm});
            skLineSegment(sketch, "E81.3.7", {"start": v(8.53, 11.05) * mm, "end": v(8.53, 9.05) * mm});
            skLineSegment(sketch, "E81.3.8", {"start": v(8.53, 9.05) * mm, "end": v(7.83, 9.05) * mm});
            skLineSegment(sketch, "E81.3.9", {"start": v(7.83, 11.05) * mm, "end": v(7.83, 9.05) * mm});
            skLineSegment(sketch, "E81.3.10", {"start": v(11.29, 7.66) * mm, "end": v(10.64, 7.66) * mm});
            skPoint(sketch, "E81.3.11", {"position": v(10.29, 8) * mm});
            skLineSegment(sketch, "E81.3.12", {"start": v(9.94, 9) * mm, "end": v(9.94, 8.36) * mm});
            skLineSegment(sketch, "E81.3.13", {"start": v(10.64, 9) * mm, "end": v(9.94, 9) * mm});
            skLineSegment(sketch, "E81.3.14", {"start": v(10.64, 7) * mm, "end": v(9.94, 7) * mm});
            skLineSegment(sketch, "E81.3.15", {"start": v(10.64, 7.66) * mm, "end": v(10.64, 7) * mm});
            skLineSegment(sketch, "E81.3.16", {"start": v(9.94, 7.66) * mm, "end": v(9.94, 7) * mm});
            skLineSegment(sketch, "E81.3.17", {"start": v(10.64, 9) * mm, "end": v(10.64, 8.36) * mm});
            skLineSegment(sketch, "E81.anchor1", {"start": v(0, 0) * mm, "end": v(7.66, -11.29) * mm, "construction": true});
            skLineSegment(sketch, "E81.anchor2", {"start": v(0, 0) * mm, "end": v(11.29, 7.66) * mm, "construction": true});
            skSolve(sketch);
        }
        {
            var Q0;
            Q0=makeQuery(id+"F14.imprint","IMPRINT",FACE,{"disambiguationData":[TD([[makeQuery(id+"F14.imprint","IMPRINT",EDGE,{"derivedFrom":makeQuery(id+"F4.opExtrude","CAP_EDGE",EDGE,{"disambiguationData":[OSD([sQuery(id+"F3.wireOp",EDGE,"E21")])],"isStart":false})}),1.0]])]});
            var Q1;
            {var subQ4=sQuery(id+"F14.wireOp",EDGE,"E58.2");Q1=makeQuery(id+"F14.imprint","IMPRINT",FACE,{"disambiguationData":[TD([[makeQuery(id+"F14.imprint","IMPRINT",EDGE,{"derivedFrom":subQ4}),-1.0]])]});}
            var Q2;
            Q2=makeQuery(id+"F14.imprint","IMPRINT",FACE,{"disambiguationData":[TD([[makeQuery(id+"F14.imprint","IMPRINT",EDGE,{"derivedFrom":makeQuery(id+"F4.opExtrude","CAP_EDGE",EDGE,{"disambiguationData":[OSD([sQuery(id+"F3.wireOp",EDGE,"E32.3.0")])],"isStart":false})}),1.0]])]});
            var Q3;
            Q3=makeQuery(id+"F14.imprint","IMPRINT",FACE,{"disambiguationData":[TD([[makeQuery(id+"F14.imprint","IMPRINT",EDGE,{"derivedFrom":makeQuery(id+"F4.opExtrude","CAP_EDGE",EDGE,{"disambiguationData":[OSD([sQuery(id+"F3.wireOp",EDGE,"E33.bottom")])],"isStart":false})}),-1.0]])]});
            var Q4;
            Q4=makeQuery(id+"F14.imprint","IMPRINT",FACE,{"disambiguationData":[TD([[makeQuery(id+"F14.imprint","IMPRINT",EDGE,{"derivedFrom":makeQuery(id+"F4.opExtrude","CAP_EDGE",EDGE,{"disambiguationData":[OSD([sQuery(id+"F3.wireOp",EDGE,"E34.1.0.1")])],"isStart":false})}),1.0]])]});
            var Q5;
            Q5=makeQuery(id+"F14.imprint","IMPRINT",FACE,{"disambiguationData":[TD([[makeQuery(id+"F14.imprint","IMPRINT",EDGE,{"derivedFrom":makeQuery(id+"F4.opExtrude","CAP_EDGE",EDGE,{"disambiguationData":[OSD([sQuery(id+"F3.wireOp",EDGE,"E34.2.0.1")])],"isStart":false})}),1.0]])]});
            var Q6;
            Q6=makeQuery(id+"F14.imprint","IMPRINT",FACE,{"disambiguationData":[TD([[makeQuery(id+"F14.imprint","IMPRINT",EDGE,{"derivedFrom":makeQuery(id+"F4.opExtrude","CAP_EDGE",EDGE,{"disambiguationData":[OSD([sQuery(id+"F3.wireOp",EDGE,"E32.2.1")])],"isStart":false})}),-1.0]])]});
            var Q7;
            Q7=makeQuery(id+"F14.imprint","IMPRINT",FACE,{"disambiguationData":[TD([[makeQuery(id+"F14.imprint","IMPRINT",EDGE,{"derivedFrom":makeQuery(id+"F4.opExtrude","CAP_EDGE",EDGE,{"disambiguationData":[OSD([sQuery(id+"F3.wireOp",EDGE,"E32.2.0")])],"isStart":false})}),1.0]])]});
            var Q8;
            Q8=makeQuery(id+"F14.imprint","IMPRINT",FACE,{"disambiguationData":[TD([[makeQuery(id+"F14.imprint","IMPRINT",EDGE,{"derivedFrom":makeQuery(id+"F4.opExtrude","CAP_EDGE",EDGE,{"disambiguationData":[OSD([sQuery(id+"F3.wireOp",EDGE,"E32.3.1")])],"isStart":false})}),-1.0]])]});
            var Q9;
            Q9=makeQuery(id+"F14.imprint","IMPRINT",FACE,{"disambiguationData":[TD([[makeQuery(id+"F14.imprint","IMPRINT",EDGE,{"derivedFrom":makeQuery(id+"F4.opExtrude","CAP_EDGE",EDGE,{"disambiguationData":[OSD([sQuery(id+"F3.wireOp",EDGE,"E28.MirrorCS")])],"isStart":false})}),-1.0]])]});
            var Q10;
            Q10=makeQuery(id+"F14.imprint","IMPRINT",FACE,{"disambiguationData":[TD([[makeQuery(id+"F14.imprint","IMPRINT",EDGE,{"derivedFrom":makeQuery(id+"F4.opExtrude","CAP_EDGE",EDGE,{"disambiguationData":[OSD([sQuery(id+"F3.wireOp",EDGE,"E19.bottom")])],"isStart":false})}),-1.0]])]});
            var Q11;
            Q11=makeQuery(id+"F14.imprint","IMPRINT",FACE,{"disambiguationData":[TD([[makeQuery(id+"F14.imprint","IMPRINT",EDGE,{"derivedFrom":makeQuery(id+"F4.opExtrude","CAP_EDGE",EDGE,{"disambiguationData":[OSD([sQuery(id+"F3.wireOp",EDGE,"E20.1.0.0")])],"isStart":false})}),-1.0]])]});
            var Q12;
            Q12=makeQuery(id+"F14.imprint","IMPRINT",FACE,{"disambiguationData":[TD([[makeQuery(id+"F14.imprint","IMPRINT",EDGE,{"derivedFrom":makeQuery(id+"F4.opExtrude","CAP_EDGE",EDGE,{"disambiguationData":[OSD([sQuery(id+"F3.wireOp",EDGE,"E32.1.0")])],"isStart":false})}),1.0]])]});
            var Q13;
            Q13=makeQuery(id+"F14.imprint","IMPRINT",FACE,{"disambiguationData":[TD([[makeQuery(id+"F14.imprint","IMPRINT",EDGE,{"derivedFrom":makeQuery(id+"F4.opExtrude","CAP_EDGE",EDGE,{"disambiguationData":[OSD([sQuery(id+"F3.wireOp",EDGE,"E32.1.1")])],"isStart":false})}),-1.0]])]});
            var Q14;
            Q14=makeQuery(id+"F14.imprint","IMPRINT",FACE,{"disambiguationData":[TD([[makeQuery(id+"F14.imprint","IMPRINT",EDGE,{"derivedFrom":makeQuery(id+"F4.opExtrude","CAP_EDGE",EDGE,{"disambiguationData":[OSD([sQuery(id+"F3.wireOp",EDGE,"E34.3.0.1")])],"isStart":false})}),1.0]])]});
            extrude(context, id + "F15", {"entities" : qUnion([Q0, Q1, Q2, Q3, Q4, Q5, Q6, Q7, Q8, Q9, Q10, Q11, Q12, Q13, Q14]), "depth" : .1 * mm});
        }
    });
